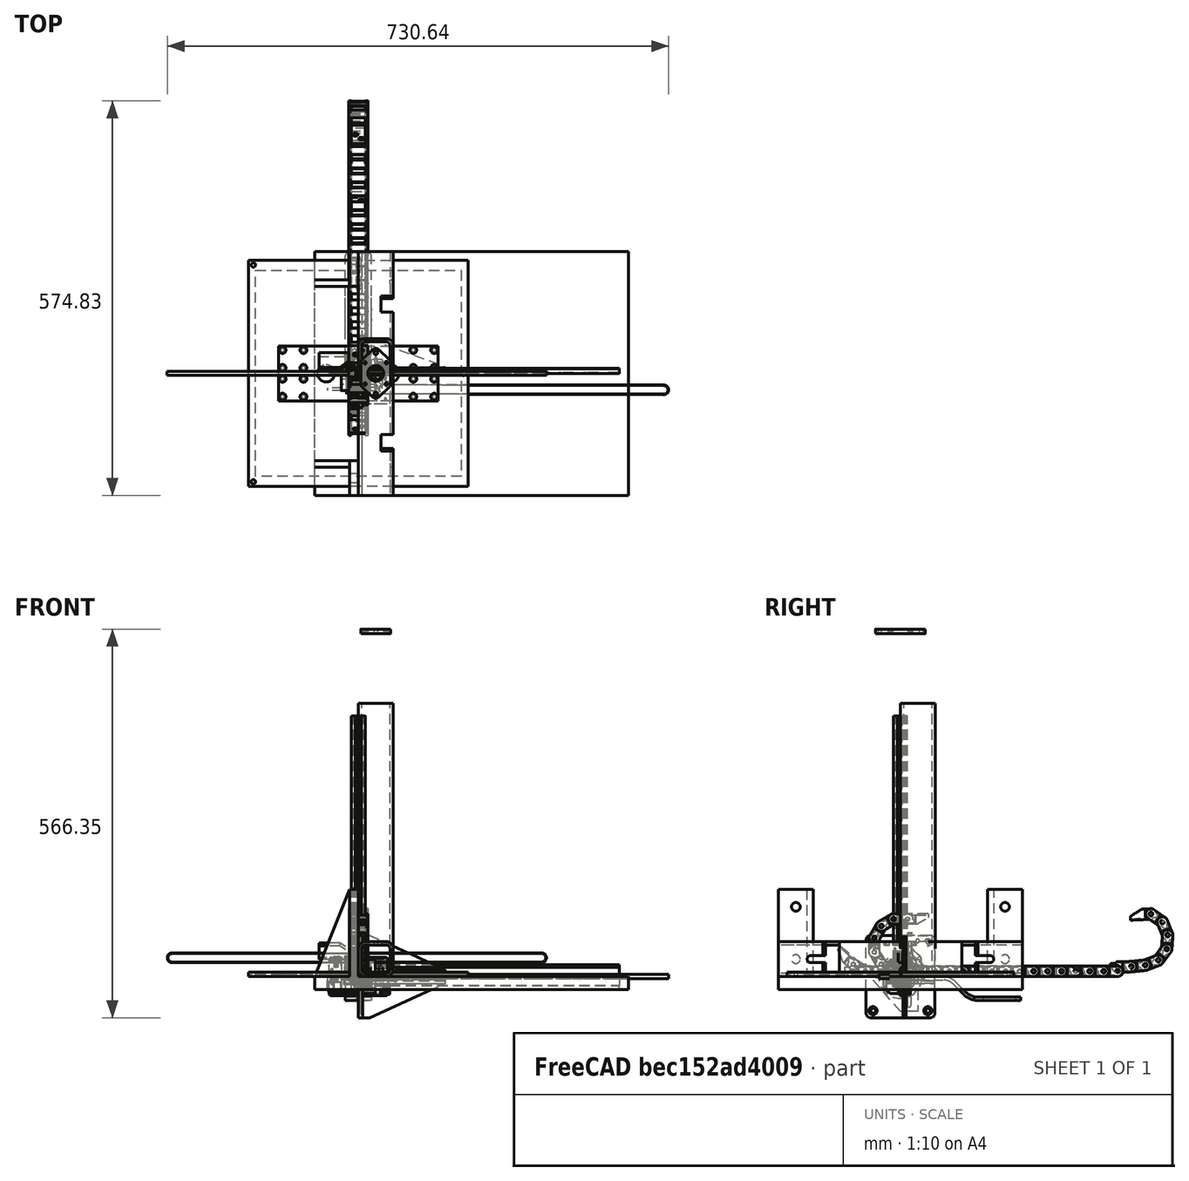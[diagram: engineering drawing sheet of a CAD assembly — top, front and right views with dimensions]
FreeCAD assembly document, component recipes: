
FREECAD ASSEMBLY — COMPONENT RECIPES ("printer_assembly")

This assembly document has 3 components, labeled P0..P2 below (a component is one placed body or linked part). 1 of them carries a construction recipe — the FreeCAD feature program that regenerates the part from scratch, quoted from this document or its linked companion documents; the rest are supplied as boundary geometry only. No exploded tour is included for this assembly.
COMPONENT P0 — recipe-attached ("Body030", modeled in this document).
Construction recipe (the document's own serialized feature program — sketch geometry with constraints, then the solid features built on it; lengths are millimeters unless a unit is written):

FEATURE [Sketcher::SketchObject] Sketch070
  MapMode = 5
  Placement = pos=(0,0,0) rot=(0.57735,0.57735,0.57735;2.0944rad)
  Support = -> [YZ_Plane083]
  sketch-geometry (13):
    g0: LineSegment StartX=12 StartY=18.65 StartZ=0 EndX=12 EndY=-18.65 EndZ=0
    g1: LineSegment StartX=5.65 StartY=-25 StartZ=0 EndX=-12 EndY=-25 EndZ=0
    g2: LineSegment StartX=-16.4901 StartY=-23.1401 StartZ=0 EndX=-24.092 EndY=-15.5382 EndZ=0
    g3: LineSegment StartX=-24.092 StartY=15.5382 StartZ=0 EndX=-16.4901 EndY=23.1401 EndZ=0
    g4: LineSegment StartX=-12 StartY=25 StartZ=0 EndX=5.65 EndY=25 EndZ=0
    g5: ArcOfCircle CenterX=5.65 CenterY=18.65 CenterZ=0 NormalX=0 NormalY=0 NormalZ=1 AngleXU=0 Radius=6.35 StartAngle=0 EndAngle=1.5708
    g6: ArcOfCircle CenterX=-12 CenterY=18.65 CenterZ=0 NormalX=0 NormalY=0 NormalZ=1 AngleXU=0 Radius=6.35 StartAngle=1.5708 EndAngle=2.35619
    g7: ArcOfCircle CenterX=-12 CenterY=-18.65 CenterZ=0 NormalX=0 NormalY=0 NormalZ=1 AngleXU=0 Radius=6.35 StartAngle=3.92699 EndAngle=4.71239
    g8: ArcOfCircle CenterX=5.65 CenterY=-18.65 CenterZ=0 NormalX=0 NormalY=0 NormalZ=1 AngleXU=0 Radius=6.35 StartAngle=4.71239 EndAngle=6.28319
    g9: Circle CenterX=-12 CenterY=0 CenterZ=0 NormalX=0 NormalY=0 NormalZ=1 AngleXU=0 Radius=4.125
    g10: LineSegment StartX=-25 StartY=13.3462 StartZ=0 EndX=-25 EndY=-13.3462 EndZ=0
    g11: ArcOfCircle CenterX=-21.9 CenterY=13.3462 CenterZ=0 NormalX=0 NormalY=0 NormalZ=1 AngleXU=0 Radius=3.1 StartAngle=2.35619 EndAngle=3.14159
    g12: ArcOfCircle CenterX=-21.9 CenterY=-13.3462 CenterZ=0 NormalX=0 NormalY=0 NormalZ=1 AngleXU=0 Radius=3.1 StartAngle=3.14159 EndAngle=3.92699
  constraints (30):
    c: Vertical(g0)
    c: Horizontal(g1)
    c: Tangent(g4,g5) = 1.5708
    c: Tangent(g0,g5) = 1.5708
    c: Tangent(g4,g6) = 1.5708
    c: Tangent(g3,g6) = 1.5708
    c: Tangent(g2,g7) = 1.5708
    c: Tangent(g1,g7) = 1.5708
    c: Tangent(g0,g8) = 1.5708
    c: Tangent(g1,g8) = 1.5708
    c: Horizontal(g4)
    c: Equal(g7,g8)
    c: Symmetric(g4,g1,g-1)
    c: Symmetric(g6,g7,g-1)
    c: PointOnObject(g9,g-1)
    c: DistanceY(g1,g4) = 50
    c: Radius(g5) = 6.35
    c: Diameter(g9) = 8.25
    c: DistanceX(g-1,g0) = 12
    c: Angle(g2,g3) = 1.5708
    c: Vertical(g10)
    c: Tangent(g3,g11) = 1.5708
    c: Tangent(g10,g11) = -1.5708
    c: Tangent(g10,g12) = -1.5708
    c: Tangent(g2,g12) = 1.5708
    c: Radius(g11) = 3.1
    c: Symmetric(g11,g12,g-1)
    c: DistanceX(g10,g-1) = 25
    c: Vertical(g7,g9)
    c: DistanceX(g9,g-1) = 12
FEATURE [PartDesign::Pad] Pad025  label="Pad026"
  Length = 50
  Length2 = 100
  Midplane = true
  Placement = pos=(0,0,0) rot=(0.57735,0.57735,0.57735;2.0944rad)
  Profile = -> Sketch070
  Type = 0
FEATURE [PartDesign::Body] Body026  label="Body030"
  Group = -> [Sketch070,Pad025]
  Origin = -> Origin083
  Tip = -> Pad025
COMPONENT P1 — geometry summary ("6541K035"; no construction recipe available for this part):
  bounding box: 9.7 x 8.4 x 6.0 mm
  tessellated surface: 668 triangles
  volume: 115 mm^3 (24% of its bounding box)
  symmetry: 2-fold rotationally symmetric about the y axis; 2-fold rotationally symmetric about the z axis; mirror-symmetric across its x mid-plane, y mid-plane, z mid-plane
COMPONENT P2 — geometry summary ("printer_assembly"; no construction recipe available for this part):
  bounding box: 598.7 x 567.9 x 565.6 mm
  tessellated surface: 103,718 triangles
  volume: 7133672 mm^3 (4% of its bounding box)
PROVENANCE & LICENSES
A FreeCAD (.FCStd) document from a public repository crawl; recipes are the document's own serialized feature recipes (and, for linked parts, companion documents' recipes).
License: as declared in the source repository (recorded in the dataset sidecar).
